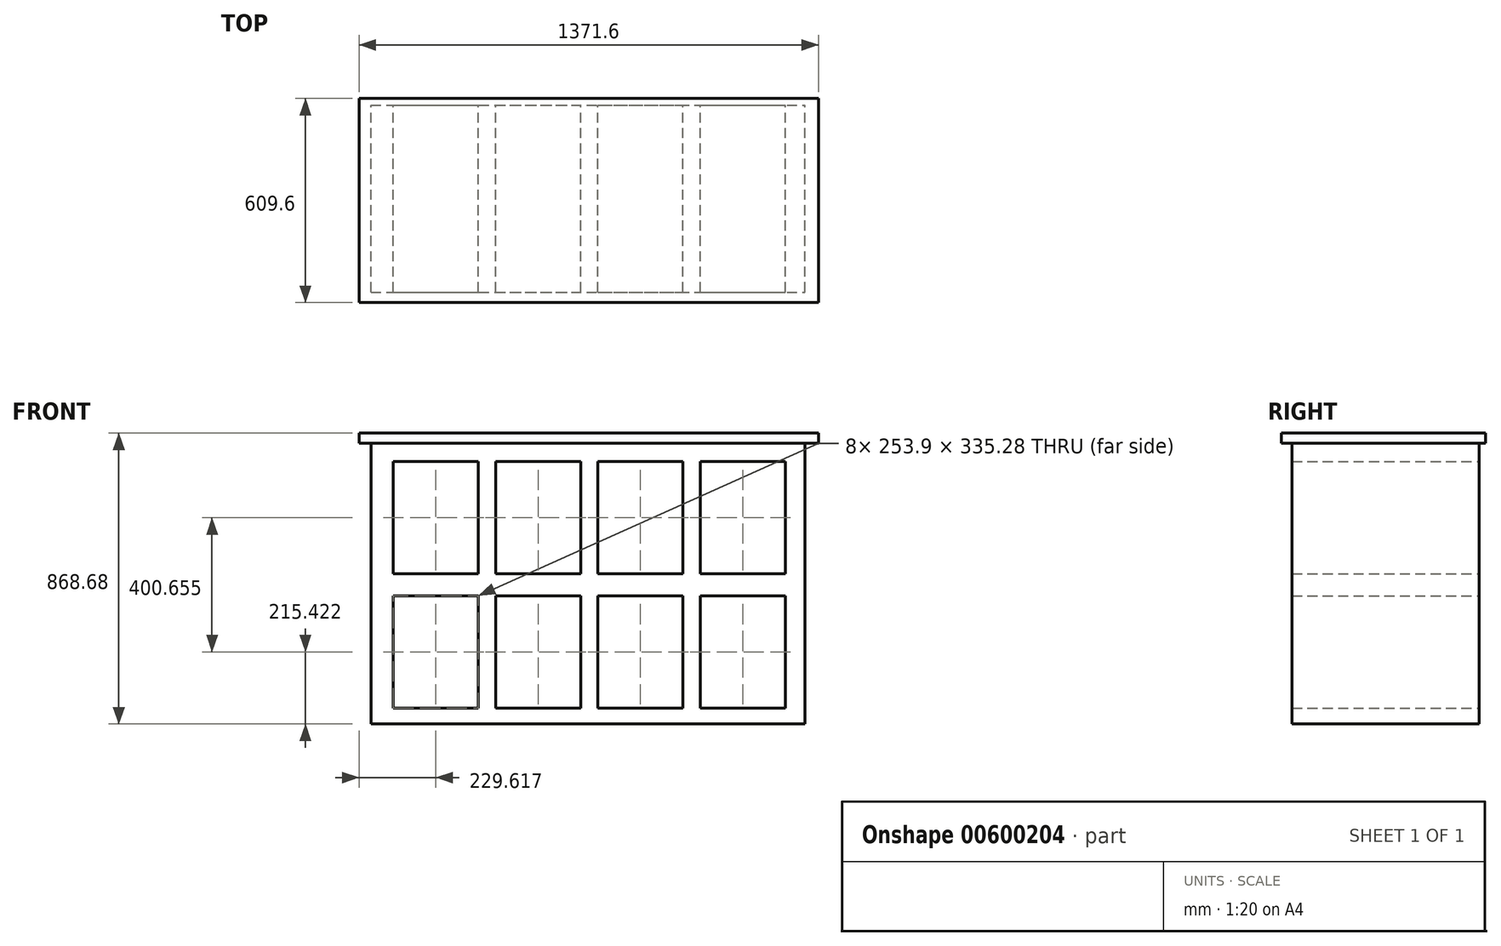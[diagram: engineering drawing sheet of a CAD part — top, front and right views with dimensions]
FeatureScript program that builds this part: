
annotation { "Feature Type Name" : "Feature", "Feature Type Description" : "" }
export const myFeature = defineFeature(function(context is Context, id is Id, definition is map)
    precondition{}
    {
        {
            var Q0;
            Q0=qCreatedBy(makeId("Front.planeOp"),FACE);
            var sketch = newSketch(context, id + "F0", { "sketchPlane" : qUnion([Q0])});
            skLineSegment(sketch, "E0.bottom", {"start": v(-638.44, 0) * mm, "end": v(656.96, 0) * mm});
            skLineSegment(sketch, "E0.top", {"start": v(-638.44, -838.2) * mm, "end": v(656.96, -838.2) * mm});
            skLineSegment(sketch, "E0.left", {"start": v(-638.44, 0) * mm, "end": v(-638.44, -838.2) * mm});
            skLineSegment(sketch, "E0.right", {"start": v(656.96, 0) * mm, "end": v(656.96, -838.2) * mm});
            skLineSegment(sketch, "E1.bottom", {"start": v(-571.63, -54.48) * mm, "end": v(-317.73, -54.48) * mm});
            skLineSegment(sketch, "E1.top", {"start": v(-571.63, -389.76) * mm, "end": v(-317.73, -389.76) * mm});
            skLineSegment(sketch, "E1.left", {"start": v(-571.63, -54.48) * mm, "end": v(-571.63, -389.76) * mm});
            skLineSegment(sketch, "E1.right", {"start": v(-317.73, -54.48) * mm, "end": v(-317.73, -389.76) * mm});
            skLineSegment(sketch, "E2.0.1.0", {"start": v(-571.63, -455.14) * mm, "end": v(-317.73, -455.14) * mm});
            skLineSegment(sketch, "E2.0.1.1", {"start": v(-317.73, -455.14) * mm, "end": v(-317.73, -790.42) * mm});
            skLineSegment(sketch, "E2.0.1.2", {"start": v(-571.63, -455.14) * mm, "end": v(-571.63, -790.42) * mm});
            skLineSegment(sketch, "E2.0.1.3", {"start": v(-571.63, -790.42) * mm, "end": v(-317.73, -790.42) * mm});
            skLineSegment(sketch, "E2.1.0.0", {"start": v(-266.2, -54.48) * mm, "end": v(-12.3, -54.48) * mm});
            skLineSegment(sketch, "E2.1.0.1", {"start": v(-12.3, -54.48) * mm, "end": v(-12.3, -389.76) * mm});
            skLineSegment(sketch, "E2.1.0.2", {"start": v(-266.2, -54.48) * mm, "end": v(-266.2, -389.76) * mm});
            skLineSegment(sketch, "E2.1.0.3", {"start": v(-266.2, -389.76) * mm, "end": v(-12.3, -389.76) * mm});
            skLineSegment(sketch, "E2.1.1.0", {"start": v(-266.2, -455.14) * mm, "end": v(-12.3, -455.14) * mm});
            skLineSegment(sketch, "E2.1.1.1", {"start": v(-12.3, -455.14) * mm, "end": v(-12.3, -790.42) * mm});
            skLineSegment(sketch, "E2.1.1.2", {"start": v(-266.2, -455.14) * mm, "end": v(-266.2, -790.42) * mm});
            skLineSegment(sketch, "E2.1.1.3", {"start": v(-266.2, -790.42) * mm, "end": v(-12.3, -790.42) * mm});
            skLineSegment(sketch, "E2.2.0.0", {"start": v(39.23, -54.48) * mm, "end": v(293.13, -54.48) * mm});
            skLineSegment(sketch, "E2.2.0.1", {"start": v(293.13, -54.48) * mm, "end": v(293.13, -389.76) * mm});
            skLineSegment(sketch, "E2.2.0.2", {"start": v(39.23, -54.48) * mm, "end": v(39.23, -389.76) * mm});
            skLineSegment(sketch, "E2.2.0.3", {"start": v(39.23, -389.76) * mm, "end": v(293.13, -389.76) * mm});
            skLineSegment(sketch, "E2.2.1.0", {"start": v(39.23, -455.14) * mm, "end": v(293.13, -455.14) * mm});
            skLineSegment(sketch, "E2.2.1.1", {"start": v(293.13, -455.14) * mm, "end": v(293.13, -790.42) * mm});
            skLineSegment(sketch, "E2.2.1.2", {"start": v(39.23, -455.14) * mm, "end": v(39.23, -790.42) * mm});
            skLineSegment(sketch, "E2.2.1.3", {"start": v(39.23, -790.42) * mm, "end": v(293.13, -790.42) * mm});
            skLineSegment(sketch, "E2.3.0.0", {"start": v(344.66, -54.48) * mm, "end": v(598.56, -54.48) * mm});
            skLineSegment(sketch, "E2.3.0.1", {"start": v(598.56, -54.48) * mm, "end": v(598.56, -389.76) * mm});
            skLineSegment(sketch, "E2.3.0.2", {"start": v(344.66, -54.48) * mm, "end": v(344.66, -389.76) * mm});
            skLineSegment(sketch, "E2.3.0.3", {"start": v(344.66, -389.76) * mm, "end": v(598.56, -389.76) * mm});
            skLineSegment(sketch, "E2.3.1.0", {"start": v(344.66, -455.14) * mm, "end": v(598.56, -455.14) * mm});
            skLineSegment(sketch, "E2.3.1.1", {"start": v(598.56, -455.14) * mm, "end": v(598.56, -790.42) * mm});
            skLineSegment(sketch, "E2.3.1.2", {"start": v(344.66, -455.14) * mm, "end": v(344.66, -790.42) * mm});
            skLineSegment(sketch, "E2.3.1.3", {"start": v(344.66, -790.42) * mm, "end": v(598.56, -790.42) * mm});
            skLineSegment(sketch, "E2.direction1", {"start": v(-317.73, -389.76) * mm, "end": v(-12.3, -389.76) * mm, "construction": true});
            skLineSegment(sketch, "E2.direction2", {"start": v(-317.73, -389.76) * mm, "end": v(-317.73, -790.42) * mm, "construction": true});
            skSolve(sketch);
        }
        {
            var Q0;
            Q0 = qSketchRegion(id + "F0", true);
            extrude(context, id + "F1", {"entities" : qUnion([Q0]), "depth" : 558.7 * mm, "offsetDistance" : 30.48 * mm});
        }
        {
            var Q0;
            Q0=qCreatedBy(makeId("Top.planeOp"),FACE);
            var sketch = newSketch(context, id + "F2", { "sketchPlane" : qUnion([Q0])});
            skLineSegment(sketch, "E3.bottom", {"start": v(-674.3, -590.01) * mm, "end": v(697.3, -590.01) * mm});
            skLineSegment(sketch, "E3.top", {"start": v(-674.3, 19.59) * mm, "end": v(697.3, 19.59) * mm});
            skLineSegment(sketch, "E3.left", {"start": v(-674.3, -590.01) * mm, "end": v(-674.3, 19.59) * mm});
            skLineSegment(sketch, "E3.right", {"start": v(697.3, -590.01) * mm, "end": v(697.3, 19.59) * mm});
            skSolve(sketch);
        }
        {
            var Q0;
            Q0=makeQuery(id+"F2.imprint","IMPRINT",FACE,{"disambiguationData":[TD([[makeQuery(id+"F2.imprint","IMPRINT",EDGE,{"derivedFrom":sQuery(id+"F2.wireOp",EDGE,"E3.bottom")}),1.0]])]});
            extrude(context, id + "F3", {"entities" : qUnion([Q0]), "operationType" : NewBodyOperationType.ADD, "depth" : 30.48 * mm, "offsetDistance" : 30.48 * mm});
        }
    });
